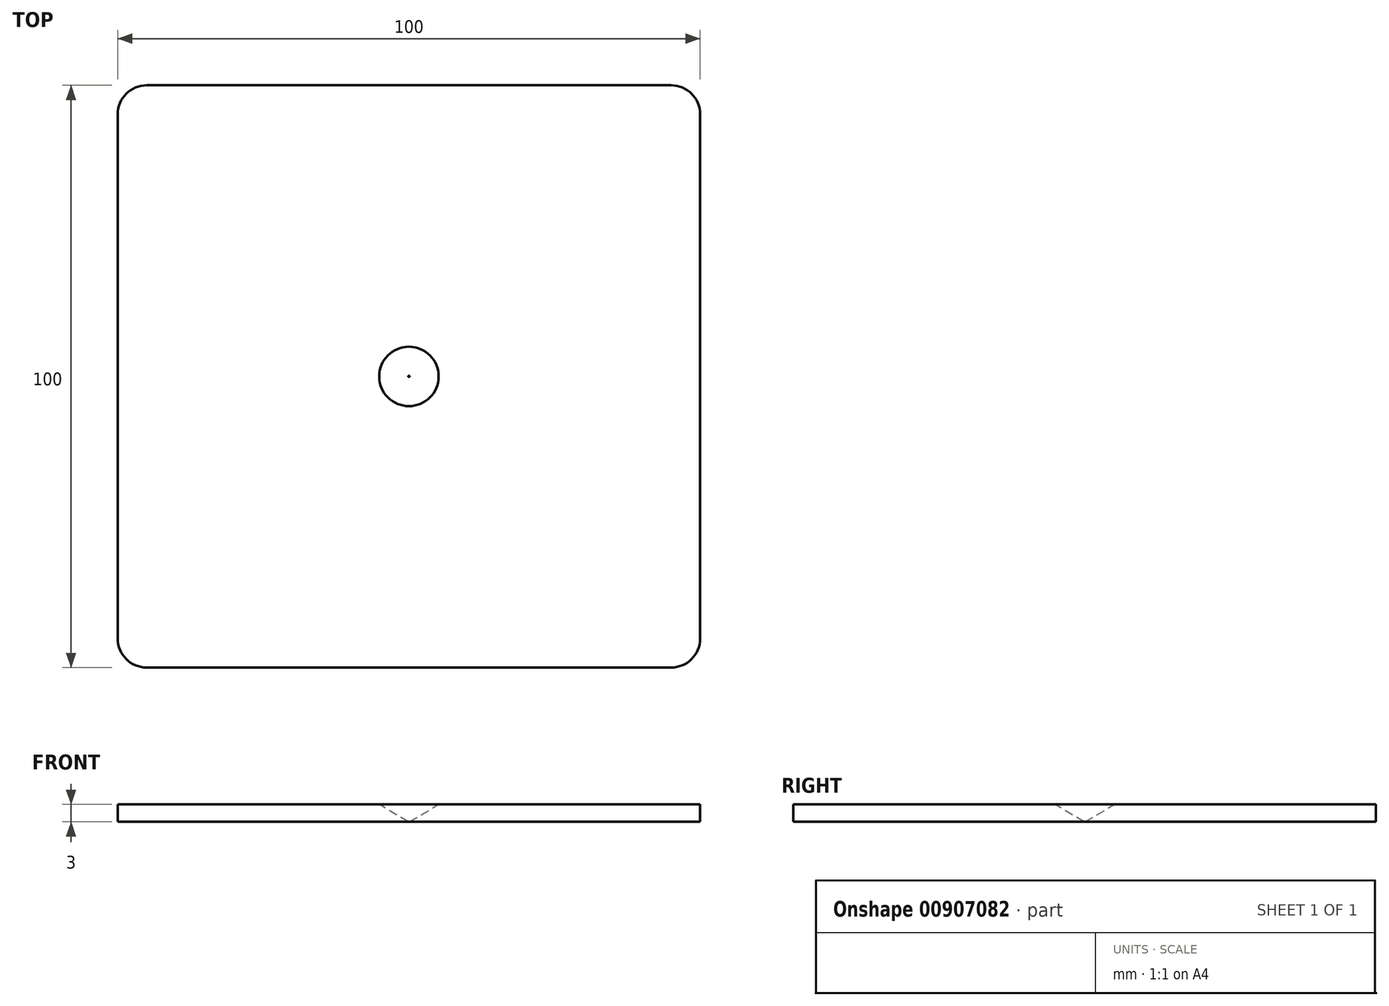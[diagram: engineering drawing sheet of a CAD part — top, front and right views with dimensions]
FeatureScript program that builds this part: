
annotation { "Feature Type Name" : "Feature", "Feature Type Description" : "" }
export const myFeature = defineFeature(function(context is Context, id is Id, definition is map)
    precondition{}
    {
        {
            var Q0;
            Q0=qCreatedBy(makeId("Top.planeOp"),FACE);
            var sketch = newSketch(context, id + "F0", { "sketchPlane" : qUnion([Q0])});
            skLineSegment(sketch, "E0.bottom", {"start": v(50, -50) * mm, "end": v(-50, -50) * mm});
            skLineSegment(sketch, "E0.top", {"start": v(50, 50) * mm, "end": v(-50, 50) * mm});
            skLineSegment(sketch, "E0.left", {"start": v(50, -50) * mm, "end": v(50, 50) * mm});
            skLineSegment(sketch, "E0.right", {"start": v(-50, -50) * mm, "end": v(-50, 50) * mm});
            skPoint(sketch, "E0.middle", {"position": v(0, 0) * mm});
            skCircle(sketch, "E1", {"center": v(0, 0) * mm, "radius": 0.1 * mm});
            skSolve(sketch);
        }
        {
            var Q0;
            Q0 = qSketchRegion(id + "F0", true);
            extrude(context, id + "F1", {"entities" : qUnion([Q0]), "depth" : 3 * mm, "offsetDistance" : 25 * mm});
        }
        {
            var Q0;
            Q0=makeQuery(id+"F1.opExtrude","CAP_EDGE",EDGE,{"disambiguationData":[OSD([sQuery(id+"F0.wireOp",EDGE,"E1")])],"isStart":false});
            chamfer(context, id + "F2", {"entities" : qUnion([Q0]), "chamferType" : ChamferType.TWO_OFFSETS, "width1" : 5 * mm, "oppositeDirection" : true, "width2" : 3 * mm, "tangentPropagation" : true});
        }
        {
            var Q0;
            Q0=makeQuery(id+"F1.opExtrude","SWEPT_EDGE",EDGE,{"disambiguationData":[OSD([sQuery(id+"F0.wireOp",EDGE,"E0.bottom"),sQuery(id+"F0.wireOp",EDGE,"E0.left")])]});
            var Q1;
            Q1=makeQuery(id+"F1.opExtrude","SWEPT_EDGE",EDGE,{"disambiguationData":[OSD([sQuery(id+"F0.wireOp",EDGE,"E0.bottom"),sQuery(id+"F0.wireOp",EDGE,"E0.right")])]});
            var Q2;
            Q2=makeQuery(id+"F1.opExtrude","SWEPT_EDGE",EDGE,{"disambiguationData":[OSD([sQuery(id+"F0.wireOp",EDGE,"E0.top"),sQuery(id+"F0.wireOp",EDGE,"E0.left")])]});
            var Q3;
            Q3=makeQuery(id+"F1.opExtrude","SWEPT_EDGE",EDGE,{"disambiguationData":[OSD([sQuery(id+"F0.wireOp",EDGE,"E0.top"),sQuery(id+"F0.wireOp",EDGE,"E0.right")])]});
            fillet(context, id + "F3", {"entities" : qUnion([Q0, Q1, Q2, Q3]), "radius" : 5 * mm, "tangentPropagation" : true, "allowEdgeOverflow" : false});
        }
    });
